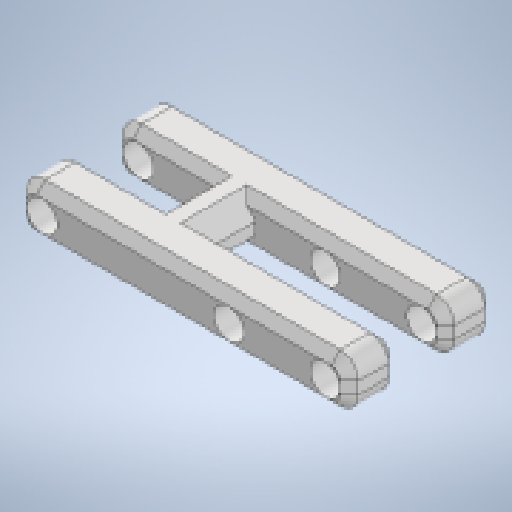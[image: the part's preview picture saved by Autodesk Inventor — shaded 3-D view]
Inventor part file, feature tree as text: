
AUTODESK INVENTOR PART (.ipt)
format: ipt  version: 2024.1 (Build 281209000, 209)  size: 275,968 bytes
history: native  units: mm
features: other x4, extrude x3, sketch x3, reference x3, projected_geometry x3, chamfer x2, fillet x1
ambient origin geometry x8: Origin, YZ Plane, XZ Plane, XY Plane, X Axis, Y Axis, Z Axis, Center Point
bodies: Body1 (feature_tree)
feature tree (19):
  other  "cross-beam"
  extrude  "Extrusion1"  Depth=55.0mm
  fillet  "Fillet1"  Radius=4.0mm
  extrude  "Extrusion2"  Depth=4.0mm
  extrude  "Extrusion3"  Depth=3.0mm
  chamfer  "Chamfer1"  Distance=5.0mm
  chamfer  "Chamfer2"  Distance=15.0mm
  sketch  "Sketch1"  dims[d0=8.0mm d2=55.0mm d4=4.0mm]
  reference  "Reference1"
  sketch  "Sketch2"  dims[d5=4.0mm d7=4.0mm]
  projected_geometry  "Projected Loop1"
  sketch  "Sketch3"  dims[d8=8.0mm d9=0.0mm d10=3.0mm d11=5.0mm d12=15.0mm d13=8.0mm d14=0.0mm d15=8.0mm d16=0.0mm d17=3.0mm d18=2.0mm d19=45.0deg d21=8.0mm d24=1.5mm d25=2.0mm d26=45.0deg]
  projected_geometry  "Projected Loop2"
  projected_geometry  "Projected Loop3"
  reference  "Reference2"
  reference  "Reference3"
  other  "<userpath>\Documents\0004-CAD\3D-cad-main\the-artifact\artifact-v2.iam"
  other  "artifact-v2.iam"
  other  "base:1"
